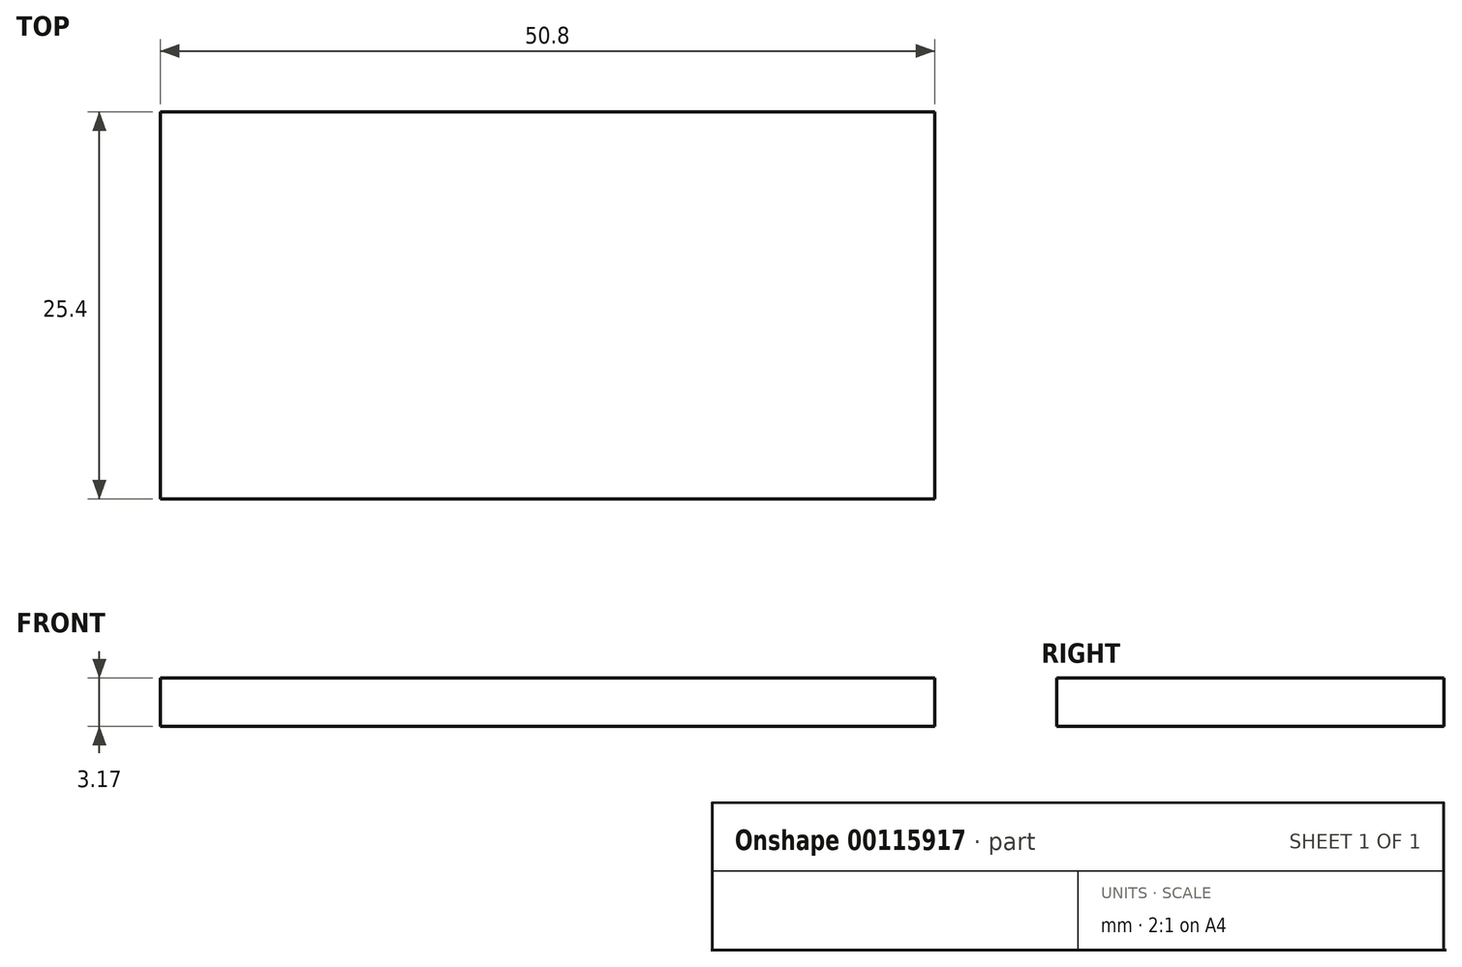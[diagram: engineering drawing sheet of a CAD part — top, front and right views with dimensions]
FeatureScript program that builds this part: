
annotation { "Feature Type Name" : "Feature", "Feature Type Description" : "" }
export const myFeature = defineFeature(function(context is Context, id is Id, definition is map)
    precondition{}
    {
        {
            var Q0;
            Q0=qCreatedBy(makeId("Top.planeOp"),FACE);
            var sketch = newSketch(context, id + "F0", { "sketchPlane" : qUnion([Q0])});
            skLineSegment(sketch, "E0.bottom", {"start": v(-39.82, 5.5) * mm, "end": v(10.98, 5.5) * mm});
            skLineSegment(sketch, "E0.top", {"start": v(-39.82, -19.9) * mm, "end": v(10.98, -19.9) * mm});
            skLineSegment(sketch, "E0.left", {"start": v(-39.82, 5.5) * mm, "end": v(-39.82, -19.9) * mm});
            skLineSegment(sketch, "E0.right", {"start": v(10.98, 5.5) * mm, "end": v(10.98, -19.9) * mm});
            skSolve(sketch);
        }
        {
            var Q0;
            Q0=makeQuery(id+"F0.imprint","IMPRINT",FACE,{"disambiguationData":[TD([[makeQuery(id+"F0.imprint","IMPRINT",EDGE,{"derivedFrom":sQuery(id+"F0.wireOp",EDGE,"E0.bottom")}),-1.0]])]});
            extrude(context, id + "F1", {"entities" : qUnion([Q0]), "depth" : 3.17 * mm});
        }
    });
